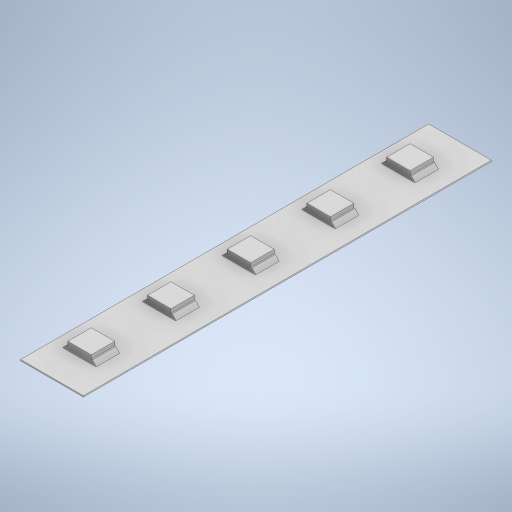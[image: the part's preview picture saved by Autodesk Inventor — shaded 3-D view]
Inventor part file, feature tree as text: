
AUTODESK INVENTOR PART (.ipt)
format: ipt  version: 2023 (Build 270158000, 158)  size: 342,016 bytes
history: native  units: in
note: dims shown in document units (in); Inventor stores cm internally (conversion verified against a paired STEP export)
features: extrude x3, sketch x2, chamfer x1
ambient origin geometry x8: Origin, YZ Plane, XZ Plane, XY Plane, X Axis, Y Axis, Z Axis, Center Point
bodies: Solid1 (feature_tree)
feature tree (6):
  extrude  "Extrusion1"  Depth=3.25in
  sketch  "Sketch2"  dims[d2=0.01in d3=0.0in d4=0.1875in d5=0.1875in d6=0.25in d7=0.125in d8=0.1875in d9=0.1875in d10=0.4475in d11=0.125in d12=0.1875in d13=0.1875in d14=0.1875in d15=0.1875in d16=0.1875in d17=0.1875in d18=0.4475in d19=0.4475in d20=0.4475in d21=0.125in d22=0.04in d23=0.04in d24=0.0625in d25=0.0in d26=0.0312in d27=0.0in d28=0.0312in d29=0.125in d30=45.0deg d31=0.1875in d32=0.1875in d33=0.1875in d34=0.1875in]
  extrude  "Extrusion2"  Depth=0.1875in
  extrude  "Extrusion3"  Depth=0.1875in
  chamfer  "Chamfer1"  Distance=0.25in
  sketch  "Sketch1"  dims[d0=0.5in d1=3.25in]
